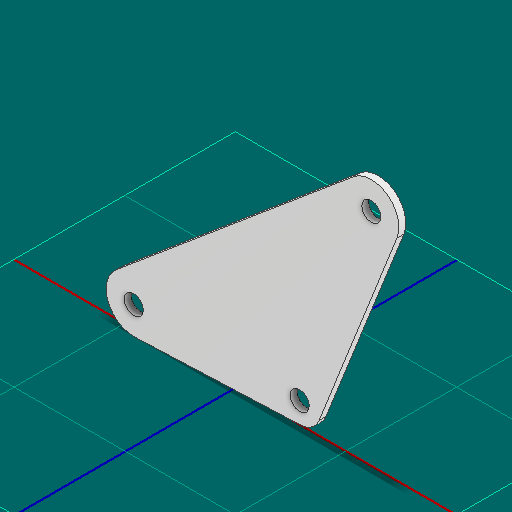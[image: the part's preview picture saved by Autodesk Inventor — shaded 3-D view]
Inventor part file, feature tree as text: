
AUTODESK INVENTOR PART (.ipt)
format: ipt  version: 2025 (Build 290162000, 162)  size: 109,568 bytes
history: native  units: in
note: dims shown in document units (in); Inventor stores cm internally (conversion verified against a paired STEP export)
features: other x3, extrude x1, sketch x1
ambient origin geometry x8: Origin, YZ Plane, XZ Plane, XY Plane, X Axis, Y Axis, Z Axis, Center Point
bodies: Body1 (feature_tree)
feature tree (5):
  other  "Blocks"
  extrude  "Extrusion2"  Depth=0.0625in TaperAngle=0.0deg
  sketch  "Sketch1"  dims[d7=0.172in d8=0.5in d9=0.375in d10=0.0625in d11=0.0in]
  other  "main"
  other  "main:1"
